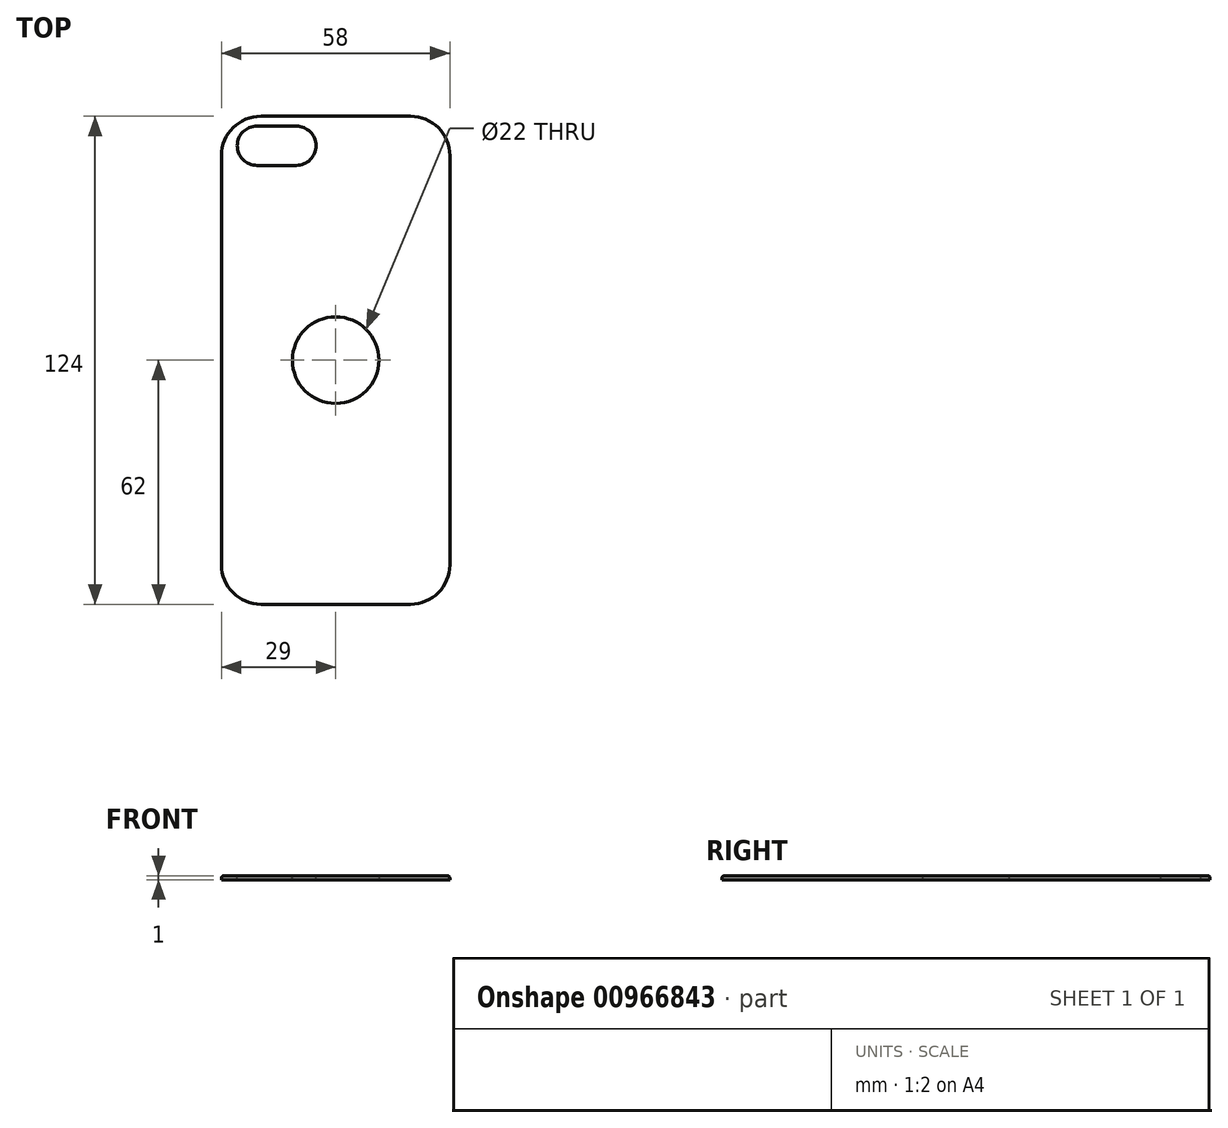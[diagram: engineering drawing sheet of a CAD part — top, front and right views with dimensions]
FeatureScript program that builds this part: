
annotation { "Feature Type Name" : "Feature", "Feature Type Description" : "" }
export const myFeature = defineFeature(function(context is Context, id is Id, definition is map)
    precondition{}
    {
        {
            var Q0;
            Q0=qCreatedBy(makeId("Top.planeOp"),FACE);
            var sketch = newSketch(context, id + "F0", { "sketchPlane" : qUnion([Q0])});
            skLineSegment(sketch, "E0.bottom", {"start": v(29, 62) * mm, "end": v(-29, 62) * mm});
            skLineSegment(sketch, "E0.top", {"start": v(29, -62) * mm, "end": v(-29, -62) * mm});
            skLineSegment(sketch, "E0.left", {"start": v(29, 62) * mm, "end": v(29, -62) * mm});
            skLineSegment(sketch, "E0.right", {"start": v(-29, 62) * mm, "end": v(-29, -62) * mm});
            skPoint(sketch, "E0.middle", {"position": v(0, 0) * mm});
            skCircle(sketch, "E1", {"center": v(0, 0) * mm, "radius": 11 * mm});
            skArc(sketch, "E2", {"start": v(-20, 59.5) * mm, "mid": v(-25, 54.5) * mm, "end": v(-20, 49.5) * mm});
            skArc(sketch, "E3", {"start": v(-10, 49.5) * mm, "mid": v(-5, 54.5) * mm, "end": v(-10, 59.5) * mm});
            skLineSegment(sketch, "E4", {"start": v(-20, 54.5) * mm, "end": v(-10, 54.5) * mm, "construction": true});
            skLineSegment(sketch, "E5", {"start": v(-20, 59.5) * mm, "end": v(-10, 59.5) * mm});
            skLineSegment(sketch, "E6", {"start": v(-20, 49.5) * mm, "end": v(-10, 49.5) * mm});
            skSolve(sketch);
        }
        {
            var Q0;
            Q0=makeQuery(id+"F0.imprint","IMPRINT",FACE,{"disambiguationData":[TD([[makeQuery(id+"F0.imprint","IMPRINT",EDGE,{"derivedFrom":sQuery(id+"F0.wireOp",EDGE,"E0.bottom")}),1.0]])]});
            extrude(context, id + "F1", {"entities" : qUnion([Q0]), "depth" : 1 * mm, "offsetDistance" : 25 * mm});
        }
        {
            var Q0;
            Q0=makeQuery(id+"F1.opExtrude","SWEPT_EDGE",EDGE,{"disambiguationData":[OSD([sQuery(id+"F0.wireOp",EDGE,"E0.top"),sQuery(id+"F0.wireOp",EDGE,"E0.right")])]});
            var Q1;
            Q1=makeQuery(id+"F1.opExtrude","SWEPT_EDGE",EDGE,{"disambiguationData":[OSD([sQuery(id+"F0.wireOp",EDGE,"E0.top"),sQuery(id+"F0.wireOp",EDGE,"E0.left")])]});
            var Q2;
            Q2=makeQuery(id+"F1.opExtrude","SWEPT_EDGE",EDGE,{"disambiguationData":[OSD([sQuery(id+"F0.wireOp",EDGE,"E0.bottom"),sQuery(id+"F0.wireOp",EDGE,"E0.left")])]});
            var Q3;
            Q3=makeQuery(id+"F1.opExtrude","SWEPT_EDGE",EDGE,{"disambiguationData":[OSD([sQuery(id+"F0.wireOp",EDGE,"E0.bottom"),sQuery(id+"F0.wireOp",EDGE,"E0.right")])]});
            fillet(context, id + "F2", {"entities" : qUnion([Q0, Q1, Q2, Q3]), "radius" : 10 * mm, "tangentPropagation" : true, "defaultsChanged" : true, "vertexSettings" : [], "allowEdgeOverflow" : false});
        }
        {
            var Q0;
            Q0=makeQuery(id+"F1.opExtrude","CAP_FACE",FACE,{"disambiguationData":[OSD([sQuery(id+"F0.wireOp",EDGE,"E0.bottom"),sQuery(id+"F0.wireOp",EDGE,"E0.top"),sQuery(id+"F0.wireOp",EDGE,"E0.left"),sQuery(id+"F0.wireOp",EDGE,"E0.right"),sQuery(id+"F0.wireOp",EDGE,"E1")])],"isStart":false});
            fillet(context, id + "F3", {"entities" : qUnion([Q0]), "radius" : 0.6 * mm, "tangentPropagation" : true, "allowEdgeOverflow" : false});
        }
    });
